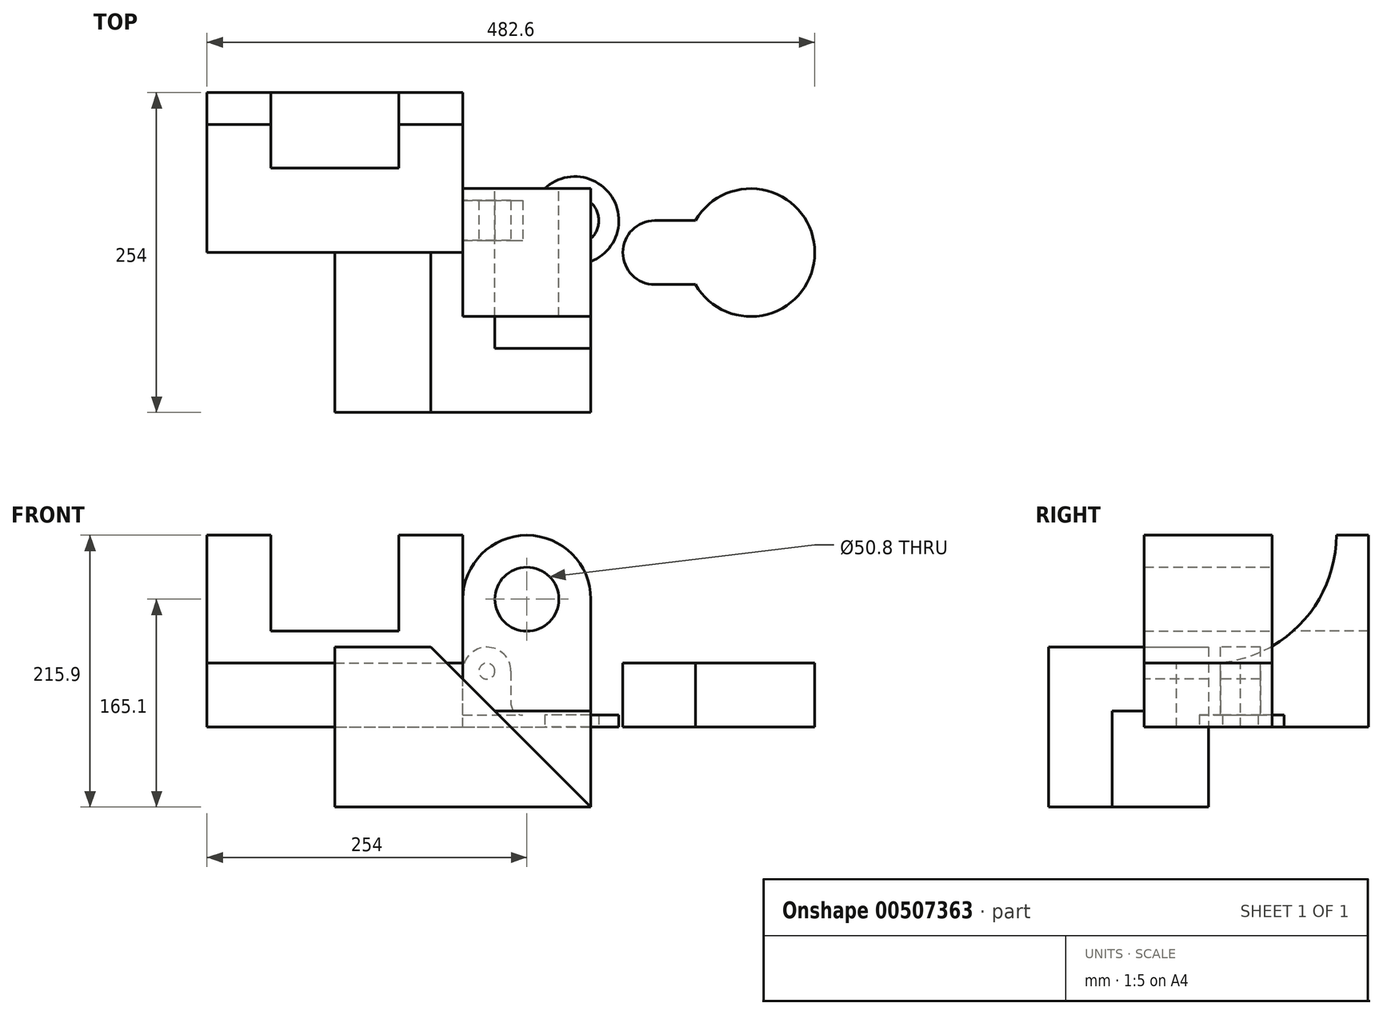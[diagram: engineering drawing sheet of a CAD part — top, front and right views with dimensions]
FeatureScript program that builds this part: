
annotation { "Feature Type Name" : "Feature", "Feature Type Description" : "" }
export const myFeature = defineFeature(function(context is Context, id is Id, definition is map)
    precondition{}
    {
        {
            var Q0;
            Q0=qCreatedBy(makeId("Front.planeOp"),FACE);
            var sketch = newSketch(context, id + "F0", { "sketchPlane" : qUnion([Q0])});
            skLineSegment(sketch, "E0.bottom", {"start": v(-101.6, 63.5) * mm, "end": v(101.6, 63.5) * mm});
            skLineSegment(sketch, "E0.top", {"start": v(-101.6, -63.5) * mm, "end": v(101.6, -63.5) * mm});
            skLineSegment(sketch, "E0.left", {"start": v(-101.6, 63.5) * mm, "end": v(-101.6, -63.5) * mm});
            skLineSegment(sketch, "E0.right", {"start": v(101.6, 63.5) * mm, "end": v(101.6, -63.5) * mm});
            skPoint(sketch, "E0.middle", {"position": v(0, 0) * mm});
            skLineSegment(sketch, "E1.bottom", {"start": v(101.6, -63.5) * mm, "end": v(25.4, -63.5) * mm});
            skLineSegment(sketch, "E1.top", {"start": v(101.6, 12.7) * mm, "end": v(25.4, 12.7) * mm});
            skLineSegment(sketch, "E1.left", {"start": v(101.6, -63.5) * mm, "end": v(101.6, 12.7) * mm});
            skPoint(sketch, "E2", {"position": v(-25.4, 63.5) * mm});
            skLineSegment(sketch, "E3", {"start": v(-25.4, 63.5) * mm, "end": v(101.6, -63.5) * mm});
            skSolve(sketch);
        }
        {
            var Q0;
            Q0=makeQuery(id+"F0.imprint","IMPRINT",FACE,{"disambiguationData":[TD([[makeQuery(id+"F0.imprint","IMPRINT",EDGE,{"derivedFrom":sQuery(id+"F0.wireOp",EDGE,"E0.top")}),1.0]])]});
            extrude(context, id + "F1", {"entities" : qUnion([Q0]), "depth" : 127 * mm, "offsetDistance" : 25.4 * mm});
        }
        {
            var Q0;
            {var subQ0=sQuery(id+"F0.wireOp",EDGE,"E1.top");Q0=makeQuery(id+"F0.imprint","IMPRINT",FACE,{"disambiguationData":[TD([[makeQuery(id+"F0.imprint","IMPRINT",EDGE,{"derivedFrom":subQ0}),1.0]])]});}
            extrude(context, id + "F2", {"entities" : qUnion([Q0]), "operationType" : NewBodyOperationType.ADD, "depth" : 76.2 * mm, "offsetDistance" : 25.4 * mm});
        }
        {
            var Q0;
            Q0=qCreatedBy(makeId("Right.planeOp"),FACE);
            var sketch = newSketch(context, id + "F3", { "sketchPlane" : qUnion([Q0])});
            skLineSegment(sketch, "E4.bottom", {"start": v(0, 0) * mm, "end": v(127, 0) * mm});
            skLineSegment(sketch, "E4.top", {"start": v(101.6, 152.4) * mm, "end": v(127, 152.4) * mm});
            skLineSegment(sketch, "E4.left", {"start": v(0, 0) * mm, "end": v(0, 50.8) * mm});
            skLineSegment(sketch, "E4.right", {"start": v(127, 0) * mm, "end": v(127, 152.4) * mm});
            skLineSegment(sketch, "E5", {"start": v(127, 76.2) * mm, "end": v(67.2, 76.2) * mm});
            skArc(sketch, "E6", {"start": v(0, 50.8) * mm, "mid": v(71.84, 80.56) * mm, "end": v(101.6, 152.4) * mm});
            skSolve(sketch);
        }
        {
            var Q0;
            Q0 = qSketchRegion(id + "F3", true);
            extrude(context, id + "F4", {"entities" : qUnion([Q0]), "oppositeDirection" : true, "depth" : 203.2 * mm, "offsetDistance" : 25.4 * mm});
        }
        {
            var Q0;
            {var subQ0=sQuery(id+"F3.wireOp",EDGE,"E4.top");Q0=makeQuery(id+"F3.imprint","IMPRINT",FACE,{"disambiguationData":[TD([[makeQuery(id+"F3.imprint","IMPRINT",EDGE,{"derivedFrom":subQ0}),-1.0]])]});}
            extrude(context, id + "F5", {"entities" : qUnion([Q0]), "operationType" : NewBodyOperationType.REMOVE, "oppositeDirection" : true, "depth" : 152.4 * mm, "offsetDistance" : 25.4 * mm, "hasSecondDirection" : true, "secondDirectionOppositeDirection" : true, "secondDirectionDepth" : 50.8 * mm});
        }
        {
            var Q0;
            Q0=qCreatedBy(makeId("Front.planeOp"),FACE);
            var sketch = newSketch(context, id + "F6", { "sketchPlane" : qUnion([Q0])});
            skLineSegment(sketch, "E7.bottom", {"start": v(0, 0) * mm, "end": v(279.4, 0) * mm});
            skLineSegment(sketch, "E7.left", {"start": v(0, 0) * mm, "end": v(0, 101.6) * mm});
            skLineSegment(sketch, "E7.right", {"start": v(279.4, 0) * mm, "end": v(279.4, 50.8) * mm});
            skArc(sketch, "E8", {"start": v(101.6, 101.6) * mm, "mid": v(50.8, 152.4) * mm, "end": v(0, 101.6) * mm});
            skLineSegment(sketch, "E9", {"start": v(101.6, 101.6) * mm, "end": v(101.6, 50.8) * mm});
            skLineSegment(sketch, "E10", {"start": v(101.6, 50.8) * mm, "end": v(279.4, 50.8) * mm});
            skCircle(sketch, "E11", {"center": v(50.8, 101.6) * mm, "radius": 25.4 * mm});
            skSolve(sketch);
        }
        {
            var Q0;
            Q0 = qSketchRegion(id + "F6", true);
            extrude(context, id + "F7", {"entities" : qUnion([Q0]), "endBound" : BoundingType.SYMMETRIC, "depth" : 101.6 * mm, "offsetDistance" : 25.4 * mm});
        }
        {
            var Q0;
            Q0=makeQuery(id+"F7.opExtrude","SWEPT_FACE",FACE,{"disambiguationData":[OSD([sQuery(id+"F6.wireOp",EDGE,"E10")])]});
            var sketch = newSketch(context, id + "F8", { "sketchPlane" : qUnion([Q0])});
            skPoint(sketch, "E12", {"position": v(152.4, 0) * mm});
            skPoint(sketch, "E13", {"position": v(228.6, 0) * mm});
            skLineSegment(sketch, "E14", {"start": v(152.4, 0) * mm, "end": v(228.6, 0) * mm});
            skArc(sketch, "E15.0.startCap", {"start": v(152.4, -25.4) * mm, "mid": v(127, 0) * mm, "end": v(152.4, 25.4) * mm});
            skArc(sketch, "E15.0.endCap", {"start": v(228.6, 25.4) * mm, "mid": v(254, 0) * mm, "end": v(228.6, -25.4) * mm});
            skLineSegment(sketch, "E15.0.left", {"start": v(152.4, 25.4) * mm, "end": v(228.6, 25.4) * mm});
            skLineSegment(sketch, "E15.0.right", {"start": v(152.4, -25.4) * mm, "end": v(228.6, -25.4) * mm});
            skArc(sketch, "E16", {"start": v(184.6, -25.4) * mm, "mid": v(279.4, 0) * mm, "end": v(184.6, 25.4) * mm});
            skSolve(sketch);
        }
        {
            var Q0;
            {var subQ4=sQuery(id+"F8.wireOp",EDGE,"E15.0.startCap");Q0=makeQuery(id+"F8.imprint","IMPRINT",FACE,{"disambiguationData":[TD([[makeQuery(id+"F8.imprint","IMPRINT",EDGE,{"derivedFrom":subQ4}),-1.0]])]});}
            var Q1;
            {var subQ0=sQuery(id+"F8.wireOp",EDGE,"E16");var subQ1=sQuery(id+"F6.wireOp",EDGE,"E10");var subQ4=makeQuery(id+"F7.opExtrude","CAP_EDGE",EDGE,{"disambiguationData":[OSD([subQ1])],"isStart":true});var subQ5=makeQuery(id+"F8.imprint","INTERSECT",VERTEX,{"derivedFrom":[subQ4,subQ0]});Q1=makeQuery(id+"F8.imprint","IMPRINT",FACE,{"disambiguationData":[TD([[makeQuery(id+"F8.imprint","IMPRINT",EDGE,{"disambiguationData":[TD([[subQ5,1.0]])],"derivedFrom":subQ0}),-1.0]])]});}
            var Q2;
            {var subQ0=sQuery(id+"F8.wireOp",EDGE,"E16");var subQ1=sQuery(id+"F6.wireOp",EDGE,"E10");var subQ2=makeQuery(id+"F7.opExtrude","CAP_EDGE",EDGE,{"disambiguationData":[OSD([subQ1])],"isStart":false});var subQ3=makeQuery(id+"F8.imprint","INTERSECT",VERTEX,{"derivedFrom":[subQ2,subQ0]});Q2=makeQuery(id+"F8.imprint","IMPRINT",FACE,{"disambiguationData":[TD([[makeQuery(id+"F8.imprint","IMPRINT",EDGE,{"disambiguationData":[TD([[subQ3,-1.0]])],"derivedFrom":subQ0}),-1.0]])]});}
            extrude(context, id + "F9", {"entities" : qUnion([Q0, Q1, Q2]), "operationType" : NewBodyOperationType.REMOVE, "oppositeDirection" : true, "depth" : 110.49 * mm, "offsetDistance" : 25.4 * mm});
        }
        {
            var Q0;
            Q0=qCreatedBy(makeId("Top.planeOp"),FACE);
            var sketch = newSketch(context, id + "F10", { "sketchPlane" : qUnion([Q0])});
            skLineSegment(sketch, "E17.bottom", {"start": v(0, 0) * mm, "end": v(64.93, 0) * mm});
            skLineSegment(sketch, "E17.top", {"start": v(0, 50.8) * mm, "end": v(64.93, 50.8) * mm});
            skLineSegment(sketch, "E17.left", {"start": v(0, 0) * mm, "end": v(0, 50.8) * mm});
            skArc(sketch, "E18", {"start": v(64.93, 0) * mm, "mid": v(123.83, 25.4) * mm, "end": v(64.93, 50.8) * mm});
            skCircle(sketch, "E19", {"center": v(88.9, 25.4) * mm, "radius": 19.05 * mm});
            skPoint(sketch, "E20.orphan", {"position": v(88.9, 50.8) * mm});
            skPoint(sketch, "E21.orphan", {"position": v(88.9, 0) * mm});
            skCircle(sketch, "E22", {"center": v(19.05, 25.4) * mm, "radius": 6.35 * mm});
            skSolve(sketch);
        }
        {
            var Q0;
            Q0=makeQuery(id+"F10.imprint","IMPRINT",FACE,{"disambiguationData":[TD([[makeQuery(id+"F10.imprint","IMPRINT",EDGE,{"derivedFrom":sQuery(id+"F10.wireOp",EDGE,"E17.bottom")}),1.0]])]});
            extrude(context, id + "F11", {"entities" : qUnion([Q0]), "depth" : 9.52 * mm, "offsetDistance" : 25.4 * mm});
        }
        {
            var Q0;
            Q0=qCreatedBy(makeId("Front.planeOp"),FACE);
            var sketch = newSketch(context, id + "F12", { "sketchPlane" : qUnion([Q0])});
            skLineSegment(sketch, "E23.0", {"start": v(0, 9.53) * mm, "end": v(47.62, 9.53) * mm});
            skLineSegment(sketch, "E24.left", {"start": v(0, 9.52) * mm, "end": v(0, 44.45) * mm});
            skArc(sketch, "E25", {"start": v(38.1, 44.45) * mm, "mid": v(19.05, 63.5) * mm, "end": v(0, 44.45) * mm});
            skLineSegment(sketch, "E26", {"start": v(38.1, 44.45) * mm, "end": v(38.1, 19.05) * mm});
            skCircle(sketch, "E27", {"center": v(19.05, 44.45) * mm, "radius": 6.35 * mm});
            skArc(sketch, "E28", {"start": v(38.1, 19.05) * mm, "mid": v(40.89, 12.31) * mm, "end": v(47.62, 9.53) * mm});
            skSolve(sketch);
        }
        {
            var Q0;
            Q0 = qSketchRegion(id + "F12", true);
            extrude(context, id + "F13", {"entities" : qUnion([Q0]), "operationType" : NewBodyOperationType.ADD, "oppositeDirection" : true, "depth" : 50.8 * mm, "offsetDistance" : 25.4 * mm});
        }
        {
            var Q0;
            Q0=makeQuery(id+"F12.imprint","IMPRINT",FACE,{"disambiguationData":[TD([[makeQuery(id+"F12.imprint","IMPRINT",EDGE,{"derivedFrom":sQuery(id+"F12.wireOp",EDGE,"E23.0")}),1.0]])]});
            extrude(context, id + "F14", {"entities" : qUnion([Q0]), "operationType" : NewBodyOperationType.REMOVE, "oppositeDirection" : true, "depth" : 41.27 * mm, "offsetDistance" : 25.4 * mm, "hasSecondDirection" : true, "secondDirectionOppositeDirection" : true, "secondDirectionDepth" : 9.52 * mm});
        }
    });
